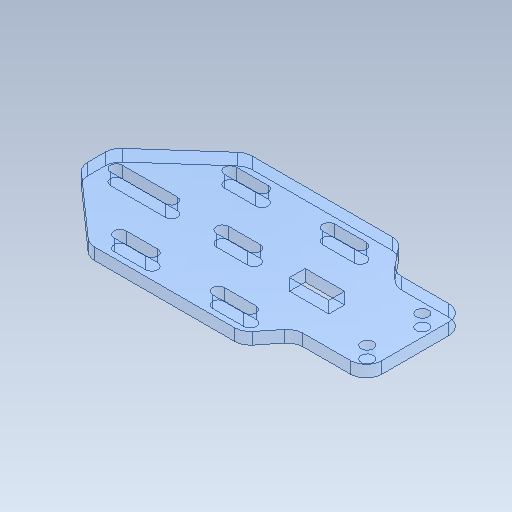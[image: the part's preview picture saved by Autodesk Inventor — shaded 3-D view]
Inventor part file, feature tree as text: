
AUTODESK INVENTOR PART (.ipt)
format: ipt  version: 2022 (Build 260153000, 153)  size: 213,504 bytes
history: native  units: mm
features: sketch x2, extrude x1
ambient origin geometry x8: Origin, YZ Plane, XZ Plane, XY Plane, X Axis, Y Axis, Z Axis, Center Point
bodies: Solid1 (feature_tree)
feature tree (3):
  sketch  "3D Sketch1"
  extrude  "Extrusion1"  [1 undecoded]
  sketch  "Sketch8"  dims[d1=3.0mm d2=0.0mm]
note: 1 required parameter value undecoded (feature->parameter linkage not recoverable at this tier; creation-order binding heuristic only, values carry confidence <= 0.55)
